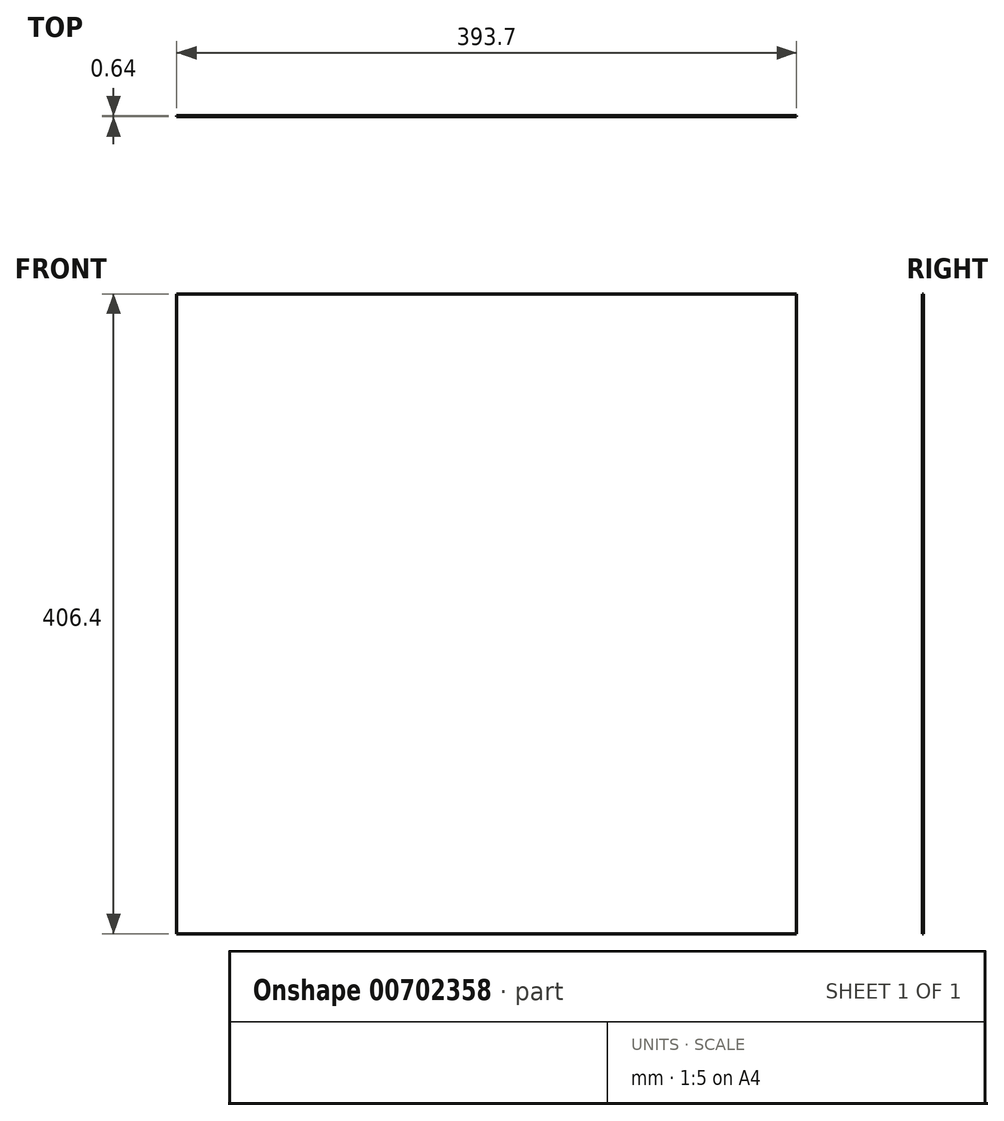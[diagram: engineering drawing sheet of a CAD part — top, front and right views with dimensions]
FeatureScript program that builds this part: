
annotation { "Feature Type Name" : "Feature", "Feature Type Description" : "" }
export const myFeature = defineFeature(function(context is Context, id is Id, definition is map)
    precondition{}
    {
        {
            var Q0;
            Q0=qCreatedBy(makeId("Front.planeOp"),FACE);
            var sketch = newSketch(context, id + "F0", { "sketchPlane" : qUnion([Q0])});
            skLineSegment(sketch, "E0.bottom", {"start": v(-196.85, 203.2) * mm, "end": v(196.85, 203.2) * mm});
            skLineSegment(sketch, "E0.top", {"start": v(-196.85, -203.2) * mm, "end": v(196.85, -203.2) * mm});
            skLineSegment(sketch, "E0.left", {"start": v(-196.85, 203.2) * mm, "end": v(-196.85, -203.2) * mm});
            skLineSegment(sketch, "E0.right", {"start": v(196.85, 203.2) * mm, "end": v(196.85, -203.2) * mm});
            skPoint(sketch, "E0.middle", {"position": v(0, 0) * mm});
            skSolve(sketch);
        }
        {
            var Q0;
            Q0=makeQuery(id+"F0.imprint","IMPRINT",FACE,{"disambiguationData":[TD([[makeQuery(id+"F0.imprint","IMPRINT",EDGE,{"derivedFrom":sQuery(id+"F0.wireOp",EDGE,"E0.bottom")}),-1.0]])]});
            extrude(context, id + "F1", {"entities" : qUnion([Q0]), "endBound" : BoundingType.SYMMETRIC, "depth" : 0.64 * mm, "offsetDistance" : 25.4 * mm});
        }
    });
